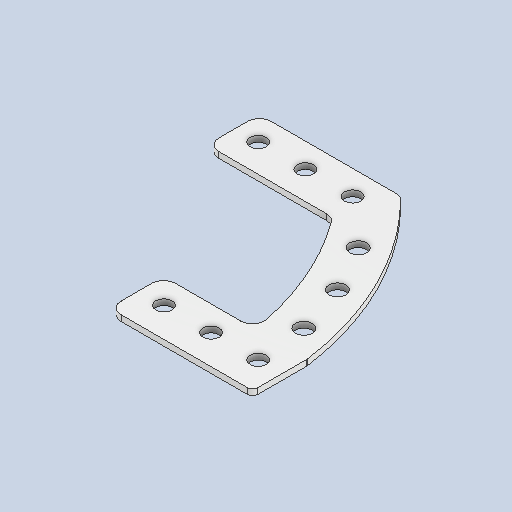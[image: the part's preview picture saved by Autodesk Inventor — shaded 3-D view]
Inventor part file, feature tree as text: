
AUTODESK INVENTOR PART (.ipt)
format: ipt  version: 2025.2 (Build 292293000, 293)  size: 139,776 bytes
history: native  units: in
note: dims shown in document units (in); Inventor stores cm internally (conversion verified against a paired STEP export)
features: other x3, sketch x1
ambient origin geometry x8: Origin, YZ Plane, XZ Plane, XY Plane, X Axis, Y Axis, Z Axis, Center Point
bodies: Solid1 (feature_tree)
feature tree (4):
  other  "Drive_Bumpers.ipt"
  other  "Solid1::Drive_Bumpers.ipt"
  other  "TaggingFeature1"
  sketch  "Sketch1"  dims[d0=0.3937in]
